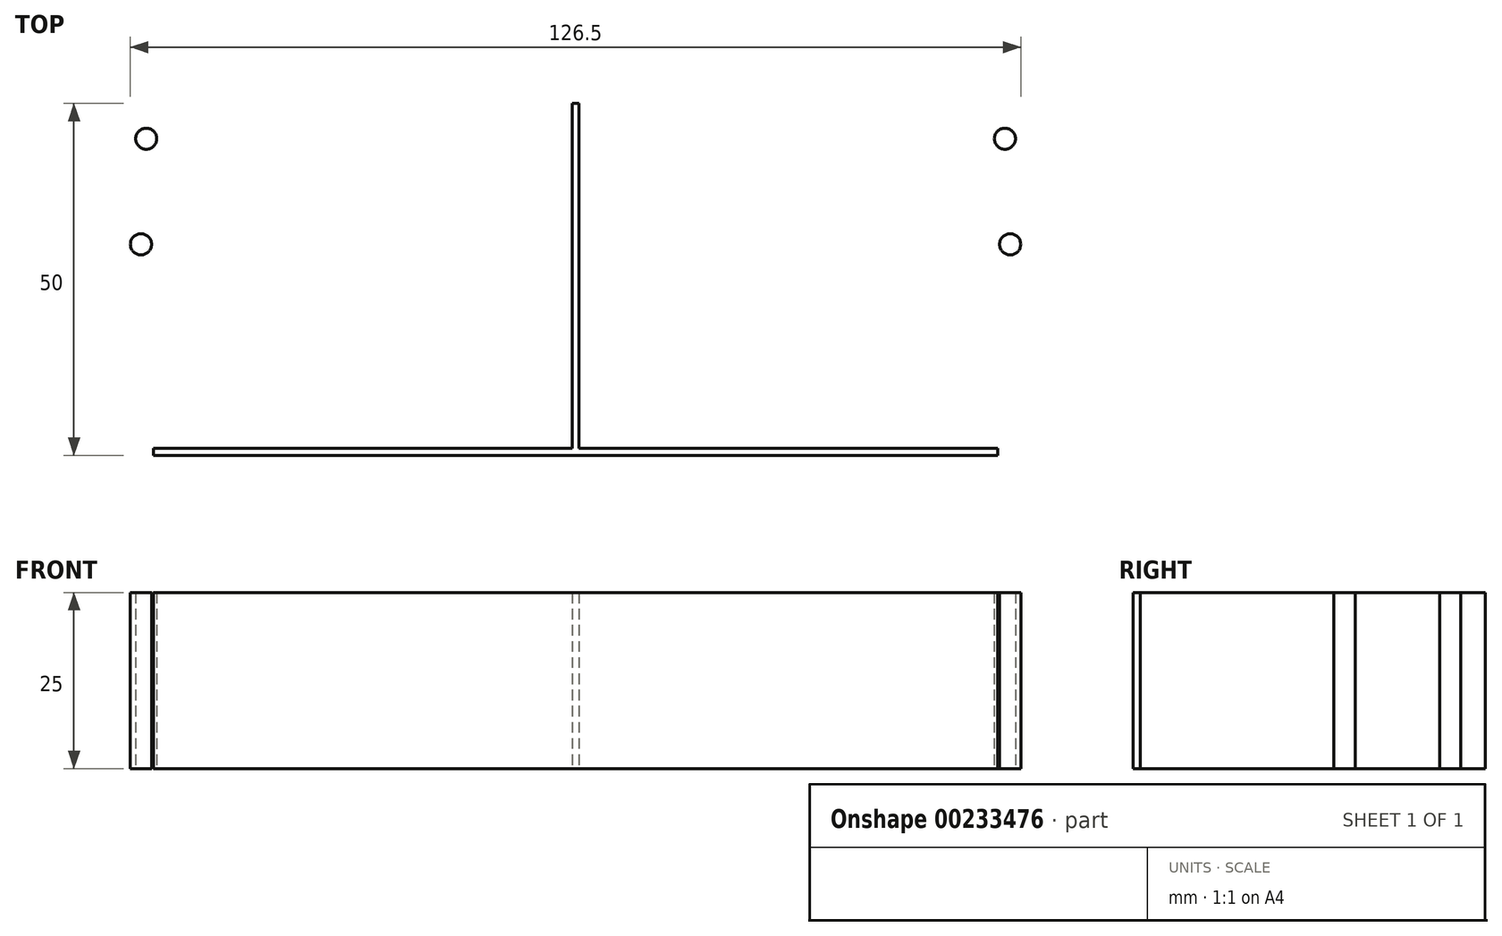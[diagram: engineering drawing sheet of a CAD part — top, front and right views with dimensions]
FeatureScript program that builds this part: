
annotation { "Feature Type Name" : "Feature", "Feature Type Description" : "" }
export const myFeature = defineFeature(function(context is Context, id is Id, definition is map)
    precondition{}
    {
        {
            var Q0;
            Q0=qCreatedBy(makeId("Top.planeOp"),FACE);
            var sketch = newSketch(context, id + "F0", { "sketchPlane" : qUnion([Q0])});
            skLineSegment(sketch, "E0.bottom", {"start": v(-0.5, 50) * mm, "end": v(0.5, 50) * mm});
            skLineSegment(sketch, "E0.top", {"start": v(-0.5, 0) * mm, "end": v(0.5, 0) * mm});
            skLineSegment(sketch, "E0.left", {"start": v(-0.5, 50) * mm, "end": v(-0.5, 0) * mm});
            skLineSegment(sketch, "E0.right", {"start": v(0.5, 50) * mm, "end": v(0.5, 0) * mm});
            skLineSegment(sketch, "E1", {"start": v(0, 0) * mm, "end": v(0, 70) * mm});
            skCircle(sketch, "E2", {"center": v(-61, 45) * mm, "radius": 1.5 * mm});
            skCircle(sketch, "E3", {"center": v(-61.75, 30) * mm, "radius": 1.5 * mm});
            skCircle(sketch, "E4.MirrorC", {"center": v(61.75, 30) * mm, "radius": 1.5 * mm});
            skCircle(sketch, "E5.MirrorC", {"center": v(61, 45) * mm, "radius": 1.5 * mm});
            skLineSegment(sketch, "E6.bottom", {"start": v(-60, 0) * mm, "end": v(60, 0) * mm});
            skLineSegment(sketch, "E6.top", {"start": v(-60, 1) * mm, "end": v(60, 1) * mm});
            skLineSegment(sketch, "E6.left", {"start": v(-60, 0) * mm, "end": v(-60, 1) * mm});
            skLineSegment(sketch, "E6.right", {"start": v(60, 0) * mm, "end": v(60, 1) * mm});
            skSolve(sketch);
        }
        {
            var Q0;
            Q0 = qSketchRegion(id + "F0", true);
            extrude(context, id + "F1", {"entities" : qUnion([Q0]), "depth" : 25 * mm, "offsetDistance" : 25 * mm});
        }
    });
